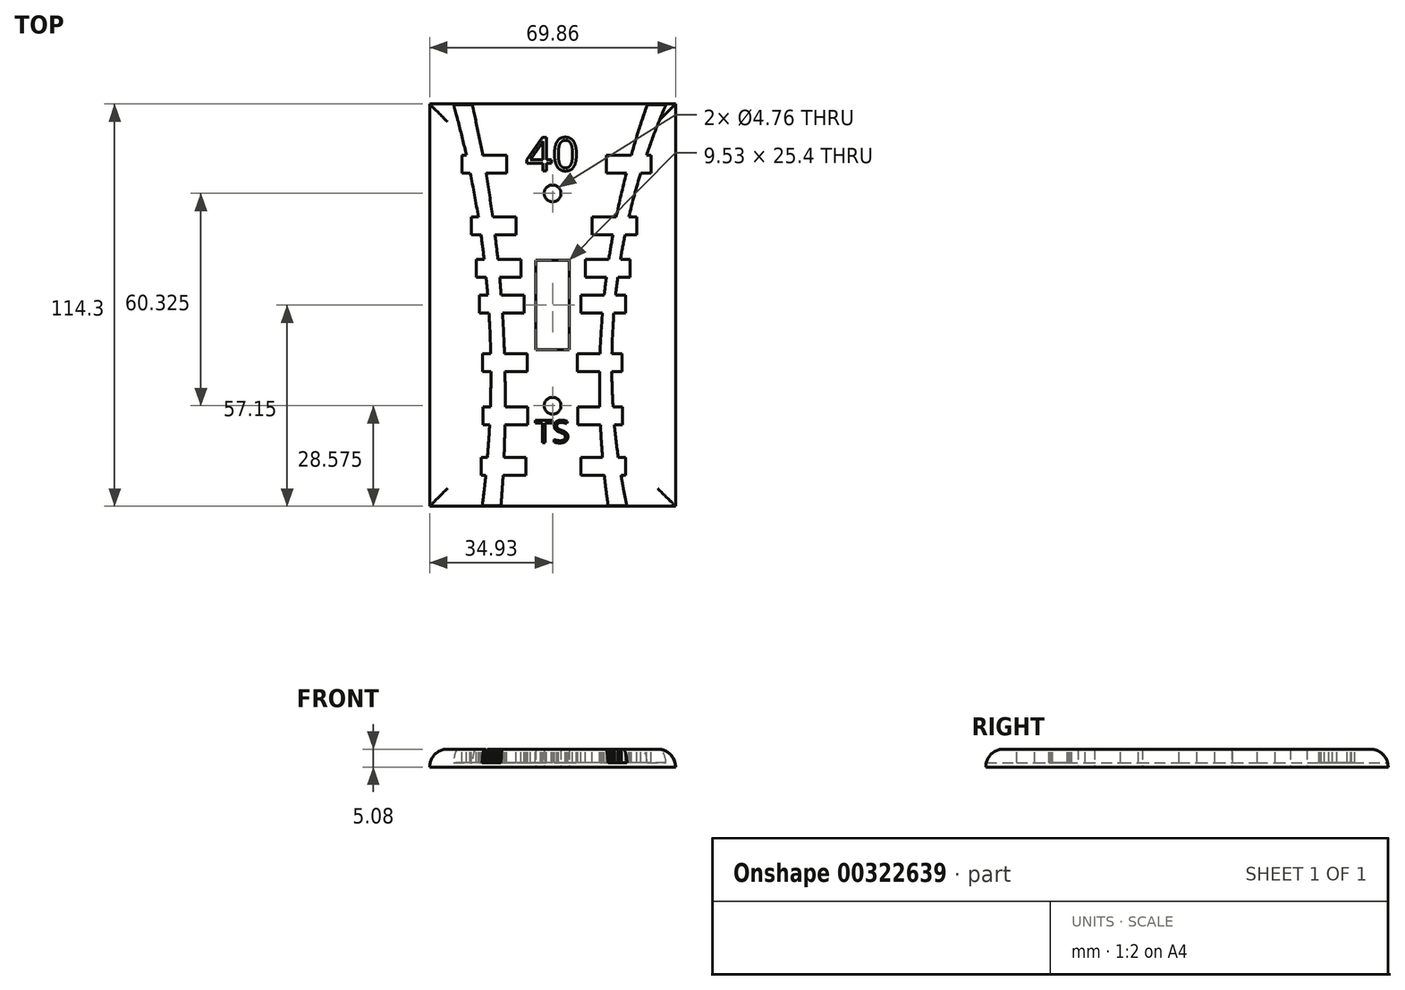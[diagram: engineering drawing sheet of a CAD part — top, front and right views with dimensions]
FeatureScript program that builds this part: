
annotation { "Feature Type Name" : "Feature", "Feature Type Description" : "" }
export const myFeature = defineFeature(function(context is Context, id is Id, definition is map)
    precondition{}
    {
        {
            var Q0;
            Q0=qCreatedBy(makeId("Top.planeOp"),FACE);
            var sketch = newSketch(context, id + "F0", { "sketchPlane" : qUnion([Q0])});
            skLineSegment(sketch, "E0", {"start": v(0, 57.15) * mm, "end": v(-34.93, 57.15) * mm});
            skLineSegment(sketch, "E1", {"start": v(-34.92, 57.15) * mm, "end": v(-34.92, 0) * mm});
            skLineSegment(sketch, "E2", {"start": v(-34.92, 0) * mm, "end": v(-34.92, -57.15) * mm});
            skLineSegment(sketch, "E3", {"start": v(-34.92, -57.15) * mm, "end": v(0, -57.15) * mm});
            skLineSegment(sketch, "E4", {"start": v(0, -57.15) * mm, "end": v(34.93, -57.15) * mm});
            skLineSegment(sketch, "E5", {"start": v(34.93, -57.15) * mm, "end": v(34.93, 0) * mm});
            skLineSegment(sketch, "E6", {"start": v(34.93, 0) * mm, "end": v(34.93, 57.15) * mm});
            skLineSegment(sketch, "E7", {"start": v(34.93, 57.15) * mm, "end": v(0, 57.15) * mm});
            skCircle(sketch, "E8", {"center": v(0, -28.58) * mm, "radius": 2.38 * mm});
            skCircle(sketch, "E9", {"center": v(0, 31.75) * mm, "radius": 2.38 * mm});
            skLineSegment(sketch, "E10.bottom", {"start": v(4.76, -12.7) * mm, "end": v(-4.76, -12.7) * mm});
            skLineSegment(sketch, "E10.top", {"start": v(4.76, 12.7) * mm, "end": v(-4.76, 12.7) * mm});
            skLineSegment(sketch, "E10.left", {"start": v(4.76, -12.7) * mm, "end": v(4.76, 12.7) * mm});
            skLineSegment(sketch, "E10.right", {"start": v(-4.76, -12.7) * mm, "end": v(-4.76, 12.7) * mm});
            skPoint(sketch, "E10.middle", {"position": v(0, 0) * mm});
            skLineSegment(sketch, "E11", {"start": v(-34.92, 0) * mm, "end": v(34.93, 0) * mm});
            skLineSegment(sketch, "E12", {"start": v(0, 57.15) * mm, "end": v(0, -57.15) * mm});
            skSolve(sketch);
        }
        {
            var Q0;
            Q0 = qSketchRegion(id + "F0", true);
            extrude(context, id + "F1", {"entities" : qUnion([Q0]), "depth" : 5.08 * mm});
        }
        {
            var Q0;
            Q0=makeQuery(id+"F1.opExtrude","CAP_FACE",FACE,{"disambiguationData":[OSD([sQuery(id+"F0.wireOp",EDGE,"E0"),sQuery(id+"F0.wireOp",EDGE,"E1"),sQuery(id+"F0.wireOp",EDGE,"E2"),sQuery(id+"F0.wireOp",EDGE,"E3"),sQuery(id+"F0.wireOp",EDGE,"E4"),sQuery(id+"F0.wireOp",EDGE,"E5"),sQuery(id+"F0.wireOp",EDGE,"E6"),sQuery(id+"F0.wireOp",EDGE,"E7"),sQuery(id+"F0.wireOp",EDGE,"E8"),sQuery(id+"F0.wireOp",EDGE,"E9"),sQuery(id+"F0.wireOp",EDGE,"E10.bottom"),sQuery(id+"F0.wireOp",EDGE,"E10.top"),sQuery(id+"F0.wireOp",EDGE,"E10.left"),sQuery(id+"F0.wireOp",EDGE,"E10.right")])],"isStart":false});
            var sketch = newSketch(context, id + "F2", { "sketchPlane" : qUnion([Q0])});
            skArc(sketch, "E13", {"start": v(-14.67, -57.15) * mm, "mid": v(-14.41, 0.31) * mm, "end": v(-22.86, 57.15) * mm});
            skArc(sketch, "E14", {"start": v(26.97, 57.15) * mm, "mid": v(14.45, 0.68) * mm, "end": v(15.8, -57.15) * mm});
            skLineSegment(sketch, "E15.bottom", {"start": v(-13.03, 37.5) * mm, "end": v(-25.73, 37.5) * mm});
            skLineSegment(sketch, "E15.top", {"start": v(-13.03, 42.57) * mm, "end": v(-25.73, 42.57) * mm});
            skLineSegment(sketch, "E15.left", {"start": v(-13.03, 37.5) * mm, "end": v(-13.03, 42.57) * mm});
            skLineSegment(sketch, "E15.right", {"start": v(-25.73, 37.5) * mm, "end": v(-25.73, 42.57) * mm});
            skPoint(sketch, "E15.middle", {"position": v(-19.38, 40.03) * mm});
            skLineSegment(sketch, "E16.bottom", {"start": v(-10.31, 19.95) * mm, "end": v(-23.01, 19.95) * mm});
            skLineSegment(sketch, "E16.top", {"start": v(-10.31, 25.03) * mm, "end": v(-23.01, 25.03) * mm});
            skLineSegment(sketch, "E16.left", {"start": v(-10.31, 19.95) * mm, "end": v(-10.31, 25.03) * mm});
            skLineSegment(sketch, "E16.right", {"start": v(-23.01, 19.95) * mm, "end": v(-23.01, 25.03) * mm});
            skPoint(sketch, "E16.middle", {"position": v(-16.66, 22.5) * mm});
            skLineSegment(sketch, "E17.bottom", {"start": v(-8.93, 7.93) * mm, "end": v(-21.63, 7.93) * mm});
            skLineSegment(sketch, "E17.top", {"start": v(-8.93, 13.01) * mm, "end": v(-21.63, 13.01) * mm});
            skLineSegment(sketch, "E17.left", {"start": v(-8.93, 7.93) * mm, "end": v(-8.93, 13.01) * mm});
            skLineSegment(sketch, "E17.right", {"start": v(-21.63, 7.93) * mm, "end": v(-21.63, 13.01) * mm});
            skPoint(sketch, "E17.middle", {"position": v(-15.28, 10.47) * mm});
            skLineSegment(sketch, "E18.bottom", {"start": v(-20.76, -2.23) * mm, "end": v(-8.06, -2.23) * mm});
            skLineSegment(sketch, "E18.top", {"start": v(-20.76, 2.85) * mm, "end": v(-8.06, 2.85) * mm});
            skLineSegment(sketch, "E18.left", {"start": v(-20.76, -2.23) * mm, "end": v(-20.76, 2.85) * mm});
            skLineSegment(sketch, "E18.right", {"start": v(-8.06, -2.23) * mm, "end": v(-8.06, 2.85) * mm});
            skPoint(sketch, "E18.middle", {"position": v(-14.41, 0.31) * mm});
            skLineSegment(sketch, "E19.bottom", {"start": v(-19.94, -18.86) * mm, "end": v(-7.24, -18.86) * mm});
            skLineSegment(sketch, "E19.top", {"start": v(-19.94, -13.78) * mm, "end": v(-7.24, -13.78) * mm});
            skLineSegment(sketch, "E19.left", {"start": v(-19.94, -18.86) * mm, "end": v(-19.94, -13.78) * mm});
            skLineSegment(sketch, "E19.right", {"start": v(-7.24, -18.86) * mm, "end": v(-7.24, -13.78) * mm});
            skPoint(sketch, "E19.middle", {"position": v(-13.6, -16.32) * mm});
            skLineSegment(sketch, "E20.bottom", {"start": v(-20.28, -48.3) * mm, "end": v(-7.58, -48.3) * mm});
            skLineSegment(sketch, "E20.top", {"start": v(-20.28, -43.21) * mm, "end": v(-7.58, -43.21) * mm});
            skLineSegment(sketch, "E20.left", {"start": v(-20.28, -48.3) * mm, "end": v(-20.28, -43.21) * mm});
            skLineSegment(sketch, "E20.right", {"start": v(-7.58, -48.3) * mm, "end": v(-7.58, -43.21) * mm});
            skPoint(sketch, "E20.middle", {"position": v(-13.93, -45.75) * mm});
            skLineSegment(sketch, "E21.bottom", {"start": v(-7.13, -34.01) * mm, "end": v(-19.83, -34.01) * mm});
            skLineSegment(sketch, "E21.top", {"start": v(-7.13, -28.93) * mm, "end": v(-19.83, -28.93) * mm});
            skLineSegment(sketch, "E21.left", {"start": v(-7.13, -34.01) * mm, "end": v(-7.13, -28.93) * mm});
            skLineSegment(sketch, "E21.right", {"start": v(-19.83, -34.01) * mm, "end": v(-19.83, -28.93) * mm});
            skPoint(sketch, "E21.middle", {"position": v(-13.48, -31.47) * mm});
            skLineSegment(sketch, "E22.bottom", {"start": v(28, 37.5) * mm, "end": v(15.3, 37.5) * mm});
            skLineSegment(sketch, "E22.top", {"start": v(28, 42.57) * mm, "end": v(15.3, 42.57) * mm});
            skLineSegment(sketch, "E22.left", {"start": v(28, 37.5) * mm, "end": v(28, 42.57) * mm});
            skLineSegment(sketch, "E22.right", {"start": v(15.3, 37.5) * mm, "end": v(15.3, 42.57) * mm});
            skPoint(sketch, "E22.middle", {"position": v(21.64, 40.03) * mm});
            skLineSegment(sketch, "E23.bottom", {"start": v(23.95, 19.95) * mm, "end": v(11.25, 19.95) * mm});
            skLineSegment(sketch, "E23.top", {"start": v(23.95, 25.03) * mm, "end": v(11.25, 25.03) * mm});
            skLineSegment(sketch, "E23.left", {"start": v(23.95, 19.95) * mm, "end": v(23.95, 25.03) * mm});
            skLineSegment(sketch, "E23.right", {"start": v(11.25, 19.95) * mm, "end": v(11.25, 25.03) * mm});
            skPoint(sketch, "E23.middle", {"position": v(17.6, 22.5) * mm});
            skPoint(sketch, "E23.middle.positionSnap0", {"position": v(-10.31, 22.5) * mm});
            skPoint(sketch, "E23.centerSnap0", {"position": v(-10.31, 22.5) * mm});
            skLineSegment(sketch, "E24.bottom", {"start": v(21.96, 7.93) * mm, "end": v(9.26, 7.93) * mm});
            skLineSegment(sketch, "E24.top", {"start": v(21.96, 13.01) * mm, "end": v(9.26, 13.01) * mm});
            skLineSegment(sketch, "E24.left", {"start": v(21.96, 7.93) * mm, "end": v(21.96, 13.01) * mm});
            skLineSegment(sketch, "E24.right", {"start": v(9.26, 7.93) * mm, "end": v(9.26, 13.01) * mm});
            skPoint(sketch, "E24.middle", {"position": v(15.6, 10.47) * mm});
            skLineSegment(sketch, "E25.bottom", {"start": v(20.76, -2.23) * mm, "end": v(8.06, -2.23) * mm});
            skLineSegment(sketch, "E25.top", {"start": v(20.76, 2.85) * mm, "end": v(8.06, 2.85) * mm});
            skLineSegment(sketch, "E25.left", {"start": v(20.76, -2.23) * mm, "end": v(20.76, 2.85) * mm});
            skLineSegment(sketch, "E25.right", {"start": v(8.06, -2.23) * mm, "end": v(8.06, 2.85) * mm});
            skPoint(sketch, "E25.middle", {"position": v(14.41, 0.31) * mm});
            skLineSegment(sketch, "E26.bottom", {"start": v(19.75, -18.86) * mm, "end": v(7.05, -18.86) * mm});
            skLineSegment(sketch, "E26.top", {"start": v(19.75, -13.78) * mm, "end": v(7.05, -13.78) * mm});
            skLineSegment(sketch, "E26.left", {"start": v(19.75, -18.86) * mm, "end": v(19.75, -13.78) * mm});
            skLineSegment(sketch, "E26.right", {"start": v(7.05, -18.86) * mm, "end": v(7.05, -13.78) * mm});
            skPoint(sketch, "E26.middle", {"position": v(13.4, -16.32) * mm});
            skLineSegment(sketch, "E27.bottom", {"start": v(20.78, -48.3) * mm, "end": v(8.08, -48.3) * mm});
            skLineSegment(sketch, "E27.top", {"start": v(20.78, -43.21) * mm, "end": v(8.08, -43.21) * mm});
            skLineSegment(sketch, "E27.left", {"start": v(20.78, -48.3) * mm, "end": v(20.78, -43.21) * mm});
            skLineSegment(sketch, "E27.right", {"start": v(8.08, -48.3) * mm, "end": v(8.08, -43.21) * mm});
            skPoint(sketch, "E27.middle", {"position": v(14.43, -45.75) * mm});
            skPoint(sketch, "E27.middle.positionSnap0", {"position": v(-7.58, -45.75) * mm});
            skPoint(sketch, "E27.centerSnap0", {"position": v(-7.58, -45.75) * mm});
            skLineSegment(sketch, "E28.bottom", {"start": v(19.83, -34.01) * mm, "end": v(7.13, -34.01) * mm});
            skLineSegment(sketch, "E28.top", {"start": v(19.83, -28.93) * mm, "end": v(7.13, -28.93) * mm});
            skLineSegment(sketch, "E28.left", {"start": v(19.83, -34.01) * mm, "end": v(19.83, -28.93) * mm});
            skLineSegment(sketch, "E28.right", {"start": v(7.13, -34.01) * mm, "end": v(7.13, -28.93) * mm});
            skPoint(sketch, "E28.middle", {"position": v(13.48, -31.47) * mm});
            skLineSegment(sketch, "E29", {"start": v(0, 0) * mm, "end": v(0, 57.15) * mm});
            skLineSegment(sketch, "E30", {"start": v(0, 0) * mm, "end": v(0, -57.15) * mm});
            skText(sketch, "E31", { "text": "TS\n", "fontName": "OpenSans-Regular.ttf"});
            skArc(sketch, "E32", {"start": v(-20, -57.15) * mm, "mid": v(-18.24, 0.42) * mm, "end": v(-28.2, 57.15) * mm});
            skArc(sketch, "E33", {"start": v(32.3, 57.15) * mm, "mid": v(17.7, 0.88) * mm, "end": v(21.14, -57.15) * mm});
            const initialGuessF2  = {"E31": [-0.00494, -0.03908, 1, 0, 0.00635]};
            skSetInitialGuess(sketch, initialGuessF2);
            skSolve(sketch);
        }
        {
            var Q0;
            {var subQ35=sQuery(id+"F2.wireOp",EDGE,"E15.left");Q0=makeQuery(id+"F2.imprint","IMPRINT",FACE,{"disambiguationData":[TD([[makeQuery(id+"F2.imprint","IMPRINT",EDGE,{"derivedFrom":subQ35}),-1.0]])]});}
            var sketch = newSketch(context, id + "F3", { "sketchPlane" : qUnion([Q0])});
            skLineSegment(sketch, "E34", {"start": v(0, 0) * mm, "end": v(0, 48.83) * mm});
            skText(sketch, "E35", { "text": "40\n\n", "fontName": "OpenSans-Regular.ttf"});
            const initialGuessF3  = {"E35": [-0.00762, 0.03819, 1, 0, 0.00947]};
            skSetInitialGuess(sketch, initialGuessF3);
            skSolve(sketch);
        }
        {
            var Q0;
            Q0=makeQuery(id+"F1.opExtrude","CAP_EDGE",EDGE,{"disambiguationData":[OSD([sQuery(id+"F0.wireOp",EDGE,"E0"),sQuery(id+"F0.wireOp",EDGE,"E7")])],"isStart":false});
            var Q1;
            Q1=makeQuery(id+"F1.opExtrude","CAP_EDGE",EDGE,{"disambiguationData":[OSD([sQuery(id+"F0.wireOp",EDGE,"E1"),sQuery(id+"F0.wireOp",EDGE,"E2")])],"isStart":false});
            var Q2;
            Q2=makeQuery(id+"F1.opExtrude","CAP_EDGE",EDGE,{"disambiguationData":[OSD([sQuery(id+"F0.wireOp",EDGE,"E5"),sQuery(id+"F0.wireOp",EDGE,"E6")])],"isStart":false});
            var Q3;
            Q3=makeQuery(id+"F1.opExtrude","CAP_EDGE",EDGE,{"disambiguationData":[OSD([sQuery(id+"F0.wireOp",EDGE,"E3"),sQuery(id+"F0.wireOp",EDGE,"E4")])],"isStart":false});
            fillet(context, id + "F4", {"entities" : qUnion([Q0, Q1, Q2, Q3]), "radius" : 5.08 * mm, "tangentPropagation" : true, "allowEdgeOverflow" : false});
        }
        {
            var Q0;
            Q0 = qSketchRegion(id + "F2", true);
            var Q1;
            {var subQ0=sQuery(id+"F2.wireOp",EDGE,"E13");var subQ3=sQuery(id+"F2.wireOp",EDGE,"E20.bottom");var subQ4=makeQuery(id+"F2.imprint","INTERSECT",VERTEX,{"derivedFrom":[subQ0,subQ3]});Q1=makeQuery(id+"F2.imprint","IMPRINT",FACE,{"disambiguationData":[TD([[makeQuery(id+"F2.imprint","IMPRINT",EDGE,{"disambiguationData":[TD([[subQ4,1.0]])],"derivedFrom":subQ3}),-1.0]])]});}
            var Q2;
            {var subQ0=sQuery(id+"F2.wireOp",EDGE,"E13");var subQ3=sQuery(id+"F2.wireOp",EDGE,"E15.top");var subQ4=makeQuery(id+"F2.imprint","INTERSECT",VERTEX,{"derivedFrom":[subQ0,subQ3]});Q2=makeQuery(id+"F2.imprint","IMPRINT",FACE,{"disambiguationData":[TD([[makeQuery(id+"F2.imprint","IMPRINT",EDGE,{"disambiguationData":[TD([[subQ4,-1.0]])],"derivedFrom":subQ3}),-1.0]])]});}
            var Q3;
            {var subQ0=sQuery(id+"F2.wireOp",EDGE,"E14");var subQ3=sQuery(id+"F2.wireOp",EDGE,"E27.bottom");var subQ4=makeQuery(id+"F2.imprint","INTERSECT",VERTEX,{"derivedFrom":[subQ0,subQ3]});Q3=makeQuery(id+"F2.imprint","IMPRINT",FACE,{"disambiguationData":[TD([[makeQuery(id+"F2.imprint","IMPRINT",EDGE,{"disambiguationData":[TD([[subQ4,1.0]])],"derivedFrom":subQ3}),1.0]])]});}
            var Q4;
            {var subQ0=sQuery(id+"F2.wireOp",EDGE,"E14");var subQ3=sQuery(id+"F2.wireOp",EDGE,"E22.top");var subQ4=makeQuery(id+"F2.imprint","INTERSECT",VERTEX,{"derivedFrom":[subQ0,subQ3]});Q4=makeQuery(id+"F2.imprint","IMPRINT",FACE,{"disambiguationData":[TD([[makeQuery(id+"F2.imprint","IMPRINT",EDGE,{"disambiguationData":[TD([[subQ4,1.0]])],"derivedFrom":subQ3}),-1.0]])]});}
            var Q5;
            Q5 = qSketchRegion(id + "F3", true);
            extrude(context, id + "F5", {"entities" : qUnion([Q0, Q1, Q2, Q3, Q4, Q5]), "operationType" : NewBodyOperationType.REMOVE, "oppositeDirection" : true, "depth" : 3.8 * mm});
        }
    });
